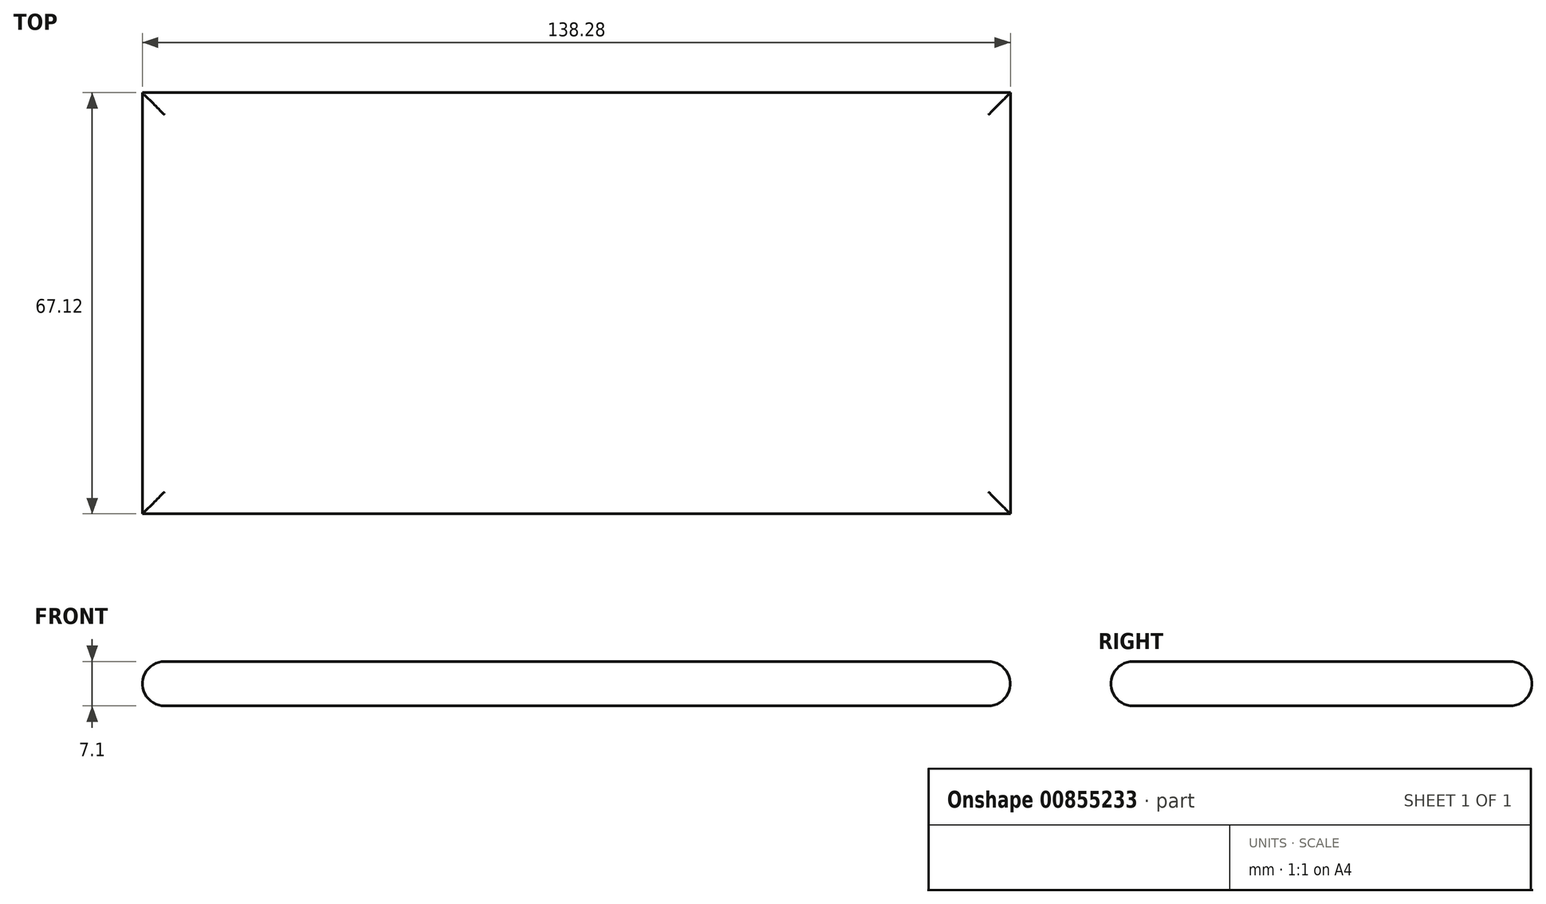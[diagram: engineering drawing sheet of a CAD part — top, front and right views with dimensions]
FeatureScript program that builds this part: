
annotation { "Feature Type Name" : "Feature", "Feature Type Description" : "" }
export const myFeature = defineFeature(function(context is Context, id is Id, definition is map)
    precondition{}
    {
        {
            var Q0;
            Q0=qCreatedBy(makeId("Top.planeOp"),FACE);
            var sketch = newSketch(context, id + "F0", { "sketchPlane" : qUnion([Q0])});
            skLineSegment(sketch, "E0.bottom", {"start": v(69.14, 33.56) * mm, "end": v(-69.14, 33.56) * mm});
            skLineSegment(sketch, "E0.top", {"start": v(69.14, -33.56) * mm, "end": v(-69.14, -33.56) * mm});
            skLineSegment(sketch, "E0.left", {"start": v(69.14, 33.56) * mm, "end": v(69.14, -33.56) * mm});
            skLineSegment(sketch, "E0.right", {"start": v(-69.14, 33.56) * mm, "end": v(-69.14, -33.56) * mm});
            skPoint(sketch, "E0.middle", {"position": v(0, 0) * mm});
            skSolve(sketch);
        }
        {
            var Q0;
            Q0 = qSketchRegion(id + "F0", true);
            extrude(context, id + "F1", {"entities" : qUnion([Q0]), "depth" : 7.1 * mm, "offsetDistance" : 25 * mm});
        }
        {
            var Q0;
            Q0=makeQuery(id+"F1.opExtrude","CAP_EDGE",EDGE,{"disambiguationData":[OSD([sQuery(id+"F0.wireOp",EDGE,"E0.top")])],"isStart":true});
            var Q1;
            Q1=makeQuery(id+"F1.opExtrude","CAP_EDGE",EDGE,{"disambiguationData":[OSD([sQuery(id+"F0.wireOp",EDGE,"E0.left")])],"isStart":false});
            var Q2;
            Q2=makeQuery(id+"F1.opExtrude","CAP_EDGE",EDGE,{"disambiguationData":[OSD([sQuery(id+"F0.wireOp",EDGE,"E0.left")])],"isStart":true});
            var Q3;
            Q3=makeQuery(id+"F1.opExtrude","CAP_EDGE",EDGE,{"disambiguationData":[OSD([sQuery(id+"F0.wireOp",EDGE,"E0.bottom")])],"isStart":false});
            var Q4;
            Q4=makeQuery(id+"F1.opExtrude","CAP_EDGE",EDGE,{"disambiguationData":[OSD([sQuery(id+"F0.wireOp",EDGE,"E0.bottom")])],"isStart":true});
            var Q5;
            Q5=makeQuery(id+"F1.opExtrude","CAP_EDGE",EDGE,{"disambiguationData":[OSD([sQuery(id+"F0.wireOp",EDGE,"E0.right")])],"isStart":false});
            var Q6;
            Q6=makeQuery(id+"F1.opExtrude","CAP_EDGE",EDGE,{"disambiguationData":[OSD([sQuery(id+"F0.wireOp",EDGE,"E0.right")])],"isStart":true});
            var Q7;
            Q7=makeQuery(id+"F1.opExtrude","CAP_EDGE",EDGE,{"disambiguationData":[OSD([sQuery(id+"F0.wireOp",EDGE,"E0.top")])],"isStart":false});
            fillet(context, id + "F2", {"entities" : qUnion([Q0, Q1, Q2, Q3, Q4, Q5, Q6, Q7]), "radius" : 3.55 * mm, "tangentPropagation" : true, "allowEdgeOverflow" : false});
        }
    });
